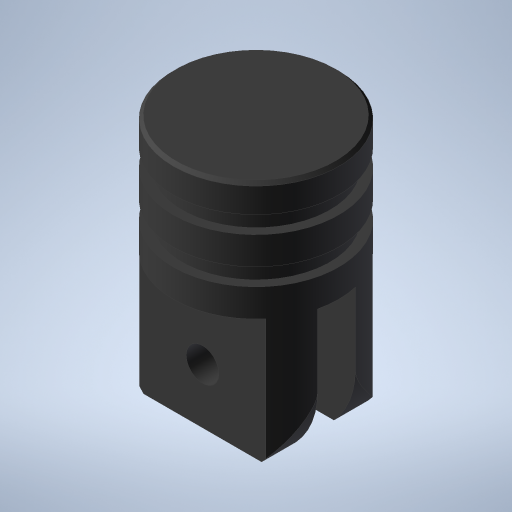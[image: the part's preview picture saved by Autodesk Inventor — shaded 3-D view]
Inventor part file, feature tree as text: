
AUTODESK INVENTOR PART (.ipt)
format: ipt  version: 2023 (Build 270158000, 158)  size: 297,984 bytes
history: native  units: in
note: dims shown in document units (in); Inventor stores cm internally (conversion verified against a paired STEP export)
features: extrude x3, sketch x3, revolve x1, chamfer x1
ambient origin geometry x8: Origin, YZ Plane, XZ Plane, XY Plane, X Axis, Y Axis, Z Axis, Center Point
bodies: Body1 (feature_tree)
feature tree (8):
  revolve  "Revolution1"  Angle=360.0deg
  chamfer  "Chamfer1"  Distance=0.025in Angle=45.0deg
  extrude  "Extrusion9"  Depth=1.313in
  sketch  "Sketch14"  dims[d77=1.0in d78=0.0in d79=0.565in d80=0.26in d81=1.0in d82=0.0in d84=0.138in d85=0.138in d86=1.0in d87=0.0in d45=0.5in d46=0.0344in d47=0.5in d48=0.0344in d73=0.5in d74=0.0344in]
  extrude  "Extrusion10"  Depth=0.565in
  extrude  "Extrusion11"  Depth=0.26in
  sketch  "Sketch5"  dims[d15=0.069in d20=360.0deg d24=0.025in d25=0.125in d26=45.0deg]
  sketch  "Sketch10"  dims[d75=0.3in d76=1.313in]
